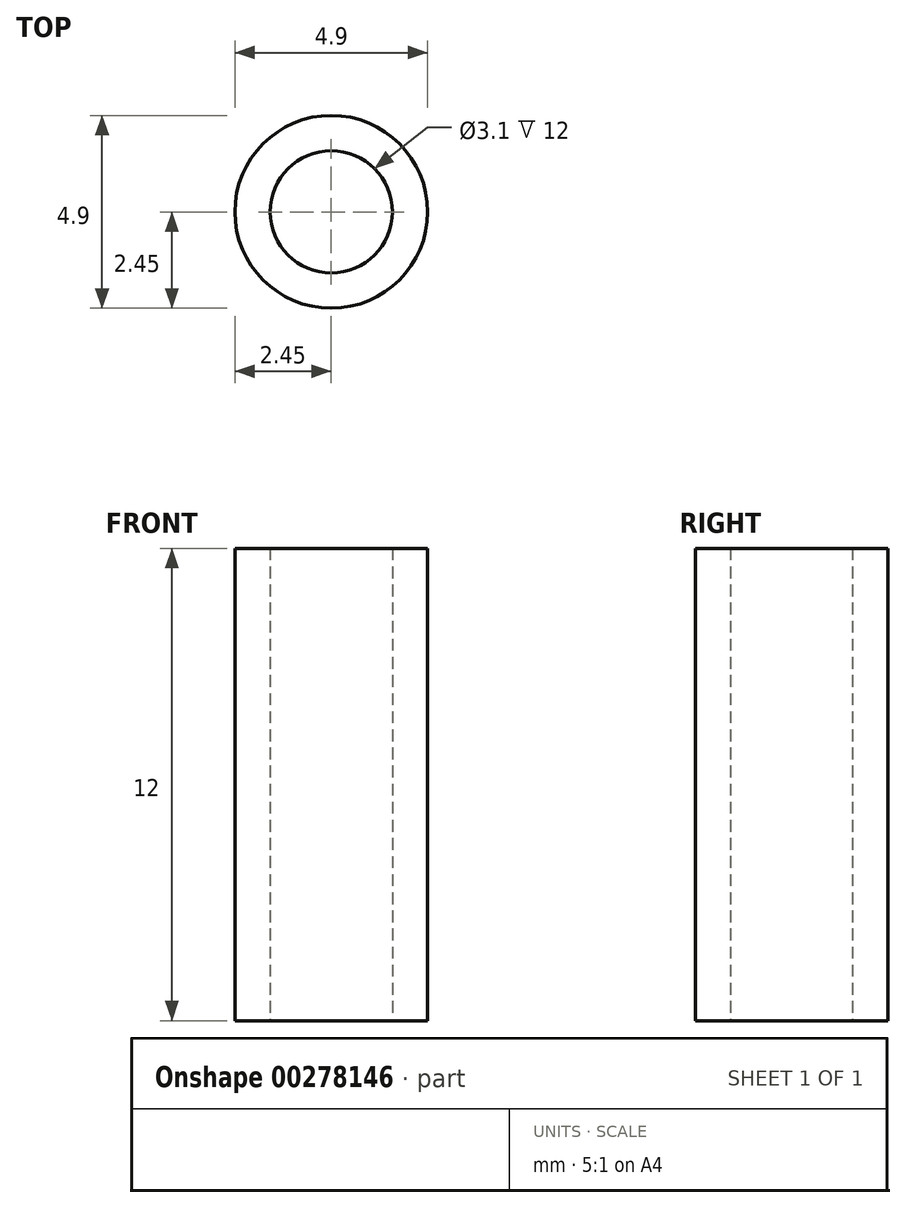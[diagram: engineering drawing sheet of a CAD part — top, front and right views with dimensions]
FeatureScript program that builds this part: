
annotation { "Feature Type Name" : "Feature", "Feature Type Description" : "" }
export const myFeature = defineFeature(function(context is Context, id is Id, definition is map)
    precondition{}
    {
        {
            var Q0;
            Q0=qCreatedBy(makeId("Top.planeOp"),FACE);
            var sketch = newSketch(context, id + "F0", { "sketchPlane" : qUnion([Q0])});
            skCircle(sketch, "E0", {"center": v(0, 0) * mm, "radius": 2.45 * mm});
            skCircle(sketch, "E1", {"center": v(0, 0) * mm, "radius": 1.55 * mm});
            skSolve(sketch);
        }
        {
            var Q0;
            Q0=makeQuery(id+"F0.imprint","IMPRINT",FACE,{"disambiguationData":[TD([[makeQuery(id+"F0.imprint","IMPRINT",EDGE,{"derivedFrom":sQuery(id+"F0.wireOp",EDGE,"E0")}),1.0]])]});
            extrude(context, id + "F1", {"entities" : qUnion([Q0]), "depth" : 12 * mm});
        }
    });
